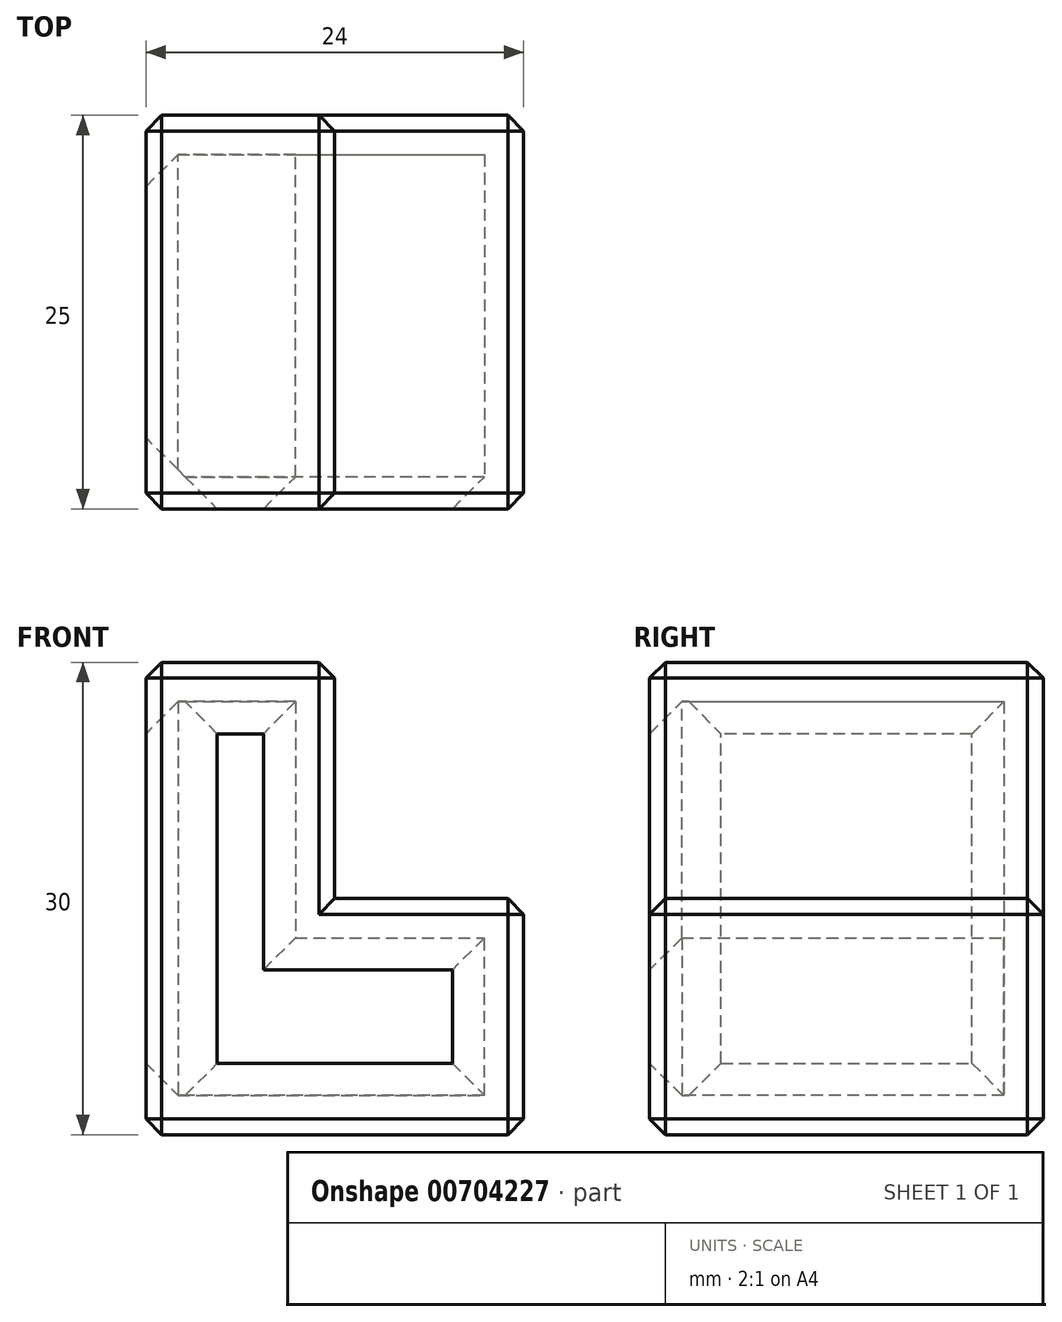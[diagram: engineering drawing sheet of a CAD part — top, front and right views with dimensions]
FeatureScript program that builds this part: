
annotation { "Feature Type Name" : "Feature", "Feature Type Description" : "" }
export const myFeature = defineFeature(function(context is Context, id is Id, definition is map)
    precondition{}
    {
        {
            var Q0;
            Q0=qCreatedBy(makeId("Front.planeOp"),FACE);
            var sketch = newSketch(context, id + "F0", { "sketchPlane" : qUnion([Q0])});
            skLineSegment(sketch, "E0", {"start": v(0, 15) * mm, "end": v(-12, 15) * mm});
            skLineSegment(sketch, "E1", {"start": v(-12, 15) * mm, "end": v(-12, -15) * mm});
            skLineSegment(sketch, "E2", {"start": v(-12, -15) * mm, "end": v(12, -15) * mm});
            skLineSegment(sketch, "E3", {"start": v(12, -15) * mm, "end": v(12, 0) * mm});
            skLineSegment(sketch, "E4", {"start": v(0, 15) * mm, "end": v(0, 0) * mm});
            skLineSegment(sketch, "E5", {"start": v(0, 0) * mm, "end": v(12, 0) * mm});
            skSolve(sketch);
        }
        {
            var Q0;
            Q0=makeQuery(id+"F0.imprint","IMPRINT",FACE,{"disambiguationData":[TD([[makeQuery(id+"F0.imprint","IMPRINT",EDGE,{"derivedFrom":sQuery(id+"F0.wireOp",EDGE,"E0")}),1.0]])]});
            extrude(context, id + "F1", {"entities" : qUnion([Q0]), "depth" : 25 * mm, "offsetDistance" : 25 * mm});
        }
        {
            var Q0;
            Q0=makeQuery(id+"F1.opExtrude","SWEPT_FACE",FACE,{"disambiguationData":[OSD([sQuery(id+"F0.wireOp",EDGE,"E0")])]});
            var Q1;
            Q1=makeQuery(id+"F1.opExtrude","CAP_FACE",FACE,{"disambiguationData":[OSD([sQuery(id+"F0.wireOp",EDGE,"E0"),sQuery(id+"F0.wireOp",EDGE,"E1"),sQuery(id+"F0.wireOp",EDGE,"E2"),sQuery(id+"F0.wireOp",EDGE,"E3"),sQuery(id+"F0.wireOp",EDGE,"E4"),sQuery(id+"F0.wireOp",EDGE,"E5")])],"isStart":false});
            var Q2;
            Q2=makeQuery(id+"F1.opExtrude","SWEPT_FACE",FACE,{"disambiguationData":[OSD([sQuery(id+"F0.wireOp",EDGE,"E3")])]});
            var Q3;
            Q3=makeQuery(id+"F1.opExtrude","SWEPT_FACE",FACE,{"disambiguationData":[OSD([sQuery(id+"F0.wireOp",EDGE,"E2")])]});
            var Q4;
            Q4=makeQuery(id+"F1.opExtrude","CAP_FACE",FACE,{"disambiguationData":[OSD([sQuery(id+"F0.wireOp",EDGE,"E0"),sQuery(id+"F0.wireOp",EDGE,"E1"),sQuery(id+"F0.wireOp",EDGE,"E2"),sQuery(id+"F0.wireOp",EDGE,"E3"),sQuery(id+"F0.wireOp",EDGE,"E4"),sQuery(id+"F0.wireOp",EDGE,"E5")])],"isStart":true});
            chamfer(context, id + "F2", {"entities" : qUnion([Q0, Q1, Q2, Q3, Q4]), "width" : 1 * mm, "tangentPropagation" : true});
        }
        {
            var Q0;
            Q0=makeQuery(id+"F1.opExtrude","SWEPT_FACE",FACE,{"disambiguationData":[OSD([sQuery(id+"F0.wireOp",EDGE,"E1")])]});
            var Q1;
            Q1=makeQuery(id+"F1.opExtrude","CAP_FACE",FACE,{"disambiguationData":[OSD([sQuery(id+"F0.wireOp",EDGE,"E0"),sQuery(id+"F0.wireOp",EDGE,"E1"),sQuery(id+"F0.wireOp",EDGE,"E2"),sQuery(id+"F0.wireOp",EDGE,"E3"),sQuery(id+"F0.wireOp",EDGE,"E4"),sQuery(id+"F0.wireOp",EDGE,"E5")])],"isStart":false});
            shell(context, id + "F3", {"entities" : qUnion([Q0, Q1]), "thickness" : 2.5 * mm});
        }
    });
